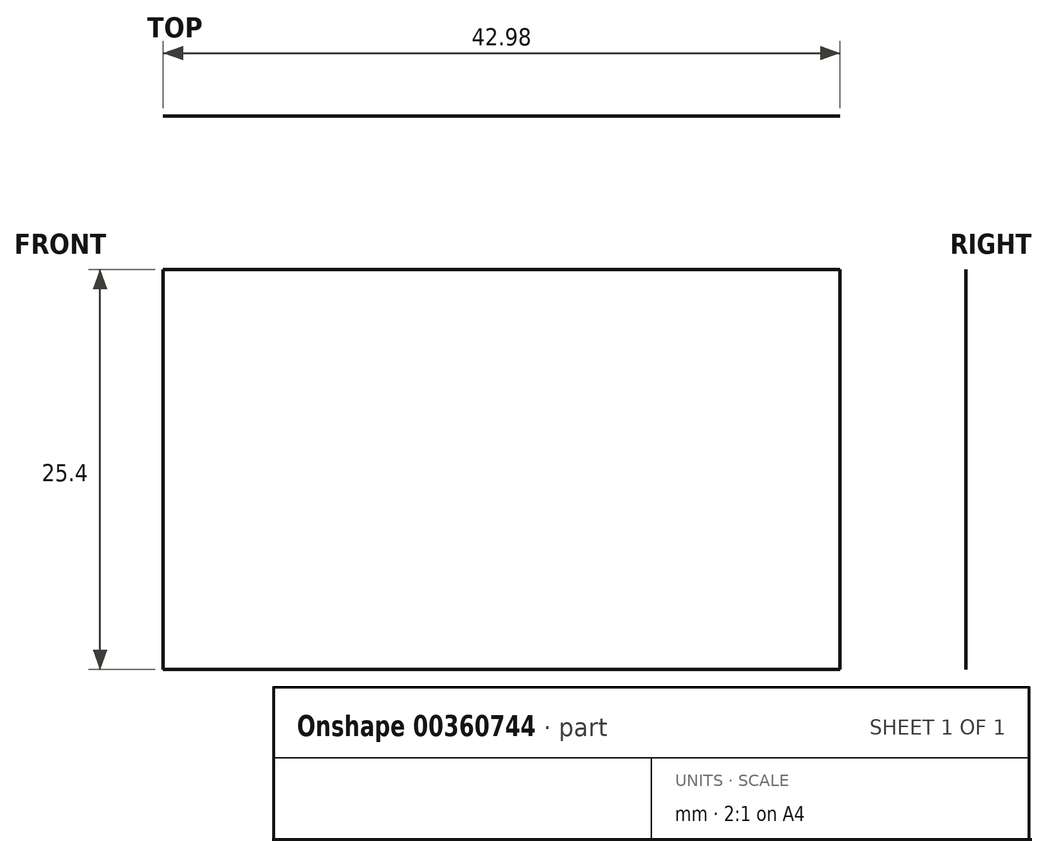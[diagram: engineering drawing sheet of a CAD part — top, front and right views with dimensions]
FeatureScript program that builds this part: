
annotation { "Feature Type Name" : "Feature", "Feature Type Description" : "" }
export const myFeature = defineFeature(function(context is Context, id is Id, definition is map)
    precondition{}
    {
        {
            var Q0;
            Q0=qCreatedBy(makeId("Top.planeOp"),FACE);
            var sketch = newSketch(context, id + "F0", { "sketchPlane" : qUnion([Q0])});
            skLineSegment(sketch, "E0.bottom", {"start": v(0, 0) * mm, "end": v(42.98, 0) * mm});
            skLineSegment(sketch, "E0.top", {"start": v(0, 26.13) * mm, "end": v(42.98, 26.13) * mm});
            skLineSegment(sketch, "E0.left", {"start": v(0, 0) * mm, "end": v(0, 26.13) * mm});
            skLineSegment(sketch, "E0.right", {"start": v(42.98, 0) * mm, "end": v(42.98, 26.13) * mm});
            skSolve(sketch);
        }
        {
            var Q0;
            Q0=sQuery(id+"F0.wireOp",EDGE,"E0.top");
            extrude(context, id + "F1", {"bodyType" : ToolBodyType.SURFACE, "surfaceEntities" : qUnion([Q0]), "oppositeDirection" : true, "depth" : 25.4 * mm});
        }
    });
